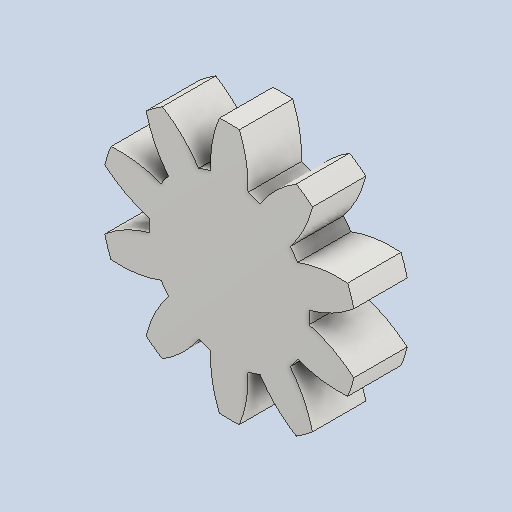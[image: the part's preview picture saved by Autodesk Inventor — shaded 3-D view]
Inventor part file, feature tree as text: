
AUTODESK INVENTOR PART (.ipt)
format: ipt  version: 2024 (Build 280153000, 153)  size: 193,536 bytes
history: native  units: mm (DEFAULTED — no unit token found)
features: plane x3, other x3, extrude x1, sketch x1
ambient origin geometry x8: Origin, YZ Plane, XZ Plane, XY Plane, X Axis, Y Axis, Z Axis, Center Point
bodies: Solid1 (feature_tree)
feature tree (8):
  extrude  "Extrusion1"  Depth=5.0mm TaperAngle=0.0deg
  plane  "Work Plane2"
  plane  "Work Plane8"
  plane  "Work Plane9"
  other  "Spur Gear"
  sketch  "Sketch1"  dims[d0=24.0mm d1=5.0mm d2=0.0mm d3=20.0mm d4=10.0mm d5=0.0mm d16=40.0mm d17=0.0mm d34=3.141593mm d39=0.0mm d41=0.0mm d43=40.0mm d46=40.0mm d47=0.0mm d48=0.0mm]
  other  "Srf1"
  other  "Pitch Diameter"
